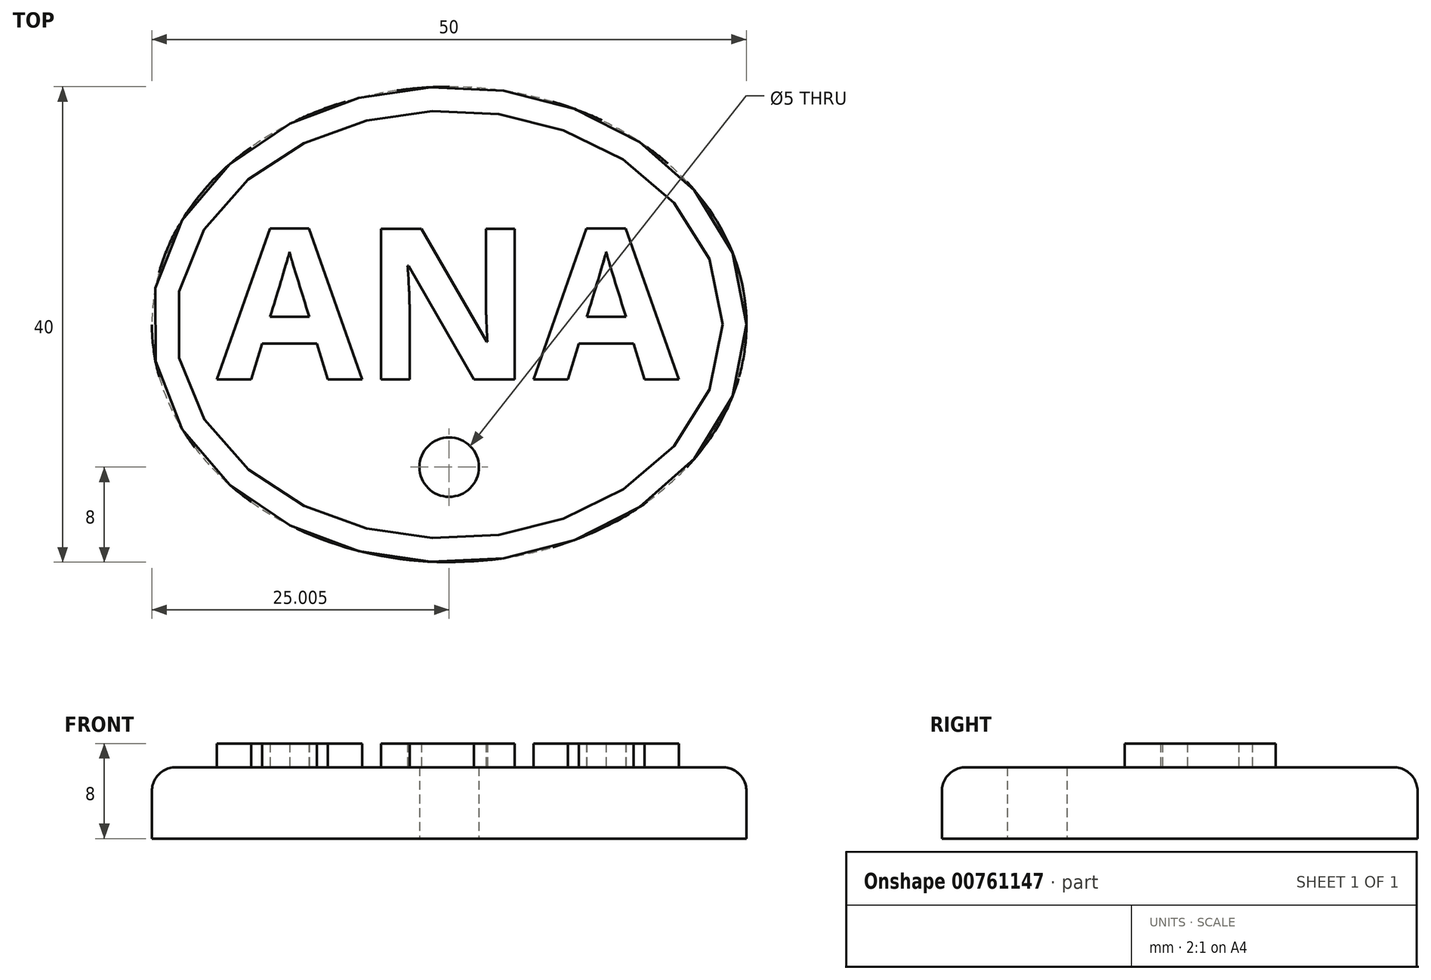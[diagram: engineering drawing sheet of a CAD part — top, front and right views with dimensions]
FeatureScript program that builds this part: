
annotation { "Feature Type Name" : "Feature", "Feature Type Description" : "" }
export const myFeature = defineFeature(function(context is Context, id is Id, definition is map)
    precondition{}
    {
        {
            var Q0;
            Q0=qCreatedBy(makeId("Top.planeOp"),FACE);
            var sketch = newSketch(context, id + "F0", { "sketchPlane" : qUnion([Q0])});
            skEllipse(sketch, "E0", {"center": v(-14.63, 0) * mm, "majorRadius": 25 * mm, "minorRadius": 20 * mm, "majorAxis": v(1, 0)});
            skLineSegment(sketch, "E1", {"start": v(-14.63, -20) * mm, "end": v(-14.63, -12) * mm});
            skCircle(sketch, "E2", {"center": v(-14.63, -12) * mm, "radius": 2.5 * mm});
            skSolve(sketch);
        }
        {
            var Q0;
            Q0 = qSketchRegion(id + "F0", true);
            extrude(context, id + "F1", {"entities" : qUnion([Q0]), "depth" : 6 * mm, "offsetDistance" : 25 * mm});
        }
        {
            var Q0;
            Q0=makeQuery(id+"F1.opExtrude","CAP_FACE",FACE,{"disambiguationData":[OSD([sQuery(id+"F0.wireOp",EDGE,"E0"),sQuery(id+"F0.wireOp",EDGE,"E2")])],"isStart":false});
            var sketch = newSketch(context, id + "F2", { "sketchPlane" : qUnion([Q0])});
            skText(sketch, "E3", { "text": "ANA", "fontName": "OpenSans-Bold.ttf"});
            const initialGuessF2  = {"E3": [-0.03417, -0.00462, 1, 0, 0.01276]};
            skSetInitialGuess(sketch, initialGuessF2);
            skSolve(sketch);
        }
        {
            var Q0;
            Q0 = qSketchRegion(id + "F2", true);
            extrude(context, id + "F3", {"entities" : qUnion([Q0]), "operationType" : NewBodyOperationType.ADD, "depth" : 2 * mm, "offsetDistance" : 25 * mm});
        }
        {
            var Q0;
            Q0=makeQuery(id+"F1.opExtrude","CAP_EDGE",EDGE,{"disambiguationData":[OSD([sQuery(id+"F0.wireOp",EDGE,"E0")])],"isStart":false});
            fillet(context, id + "F4", {"entities" : qUnion([Q0]), "radius" : 2 * mm, "tangentPropagation" : true, "allowEdgeOverflow" : false});
        }
    });
